annotation { "Feature Type Name" : "Feature", "Feature Type Description" : "" }
export const myFeature = defineFeature(function(context is Context, id is Id, definition is map)
    precondition{}
    {
        {
            var Q0;
            Q0=qCreatedBy(makeId("Front.planeOp"),FACE);
            var sketch = newSketch(context, id + "F0", { "sketchPlane" : qUnion([Q0])});
            skLineSegment(sketch, "E0", {"start": v(-61.48, 18.28) * mm, "end": v(-20.16, 18.28) * mm});
            skArc(sketch, "E1", {"start": v(-17.8, 28.55) * mm, "mid": v(-19.73, 23.59) * mm, "end": v(-20.16, 18.28) * mm});
            skArc(sketch, "E2", {"start": v(11.9, 28.55) * mm, "mid": v(-2.95, 29.61) * mm, "end": v(-17.8, 28.55) * mm});
            skArc(sketch, "E3", {"start": v(29.68, 17.53) * mm, "mid": v(21.17, 23.67) * mm, "end": v(11.9, 28.55) * mm});
            skArc(sketch, "E4", {"start": v(56.72, 13.52) * mm, "mid": v(43.38, 16.77) * mm, "end": v(29.68, 17.53) * mm});
            skArc(sketch, "E5", {"start": v(56.72, 13.52) * mm, "mid": v(57.23, 9.12) * mm, "end": v(58.87, 5) * mm});
            skArc(sketch, "E6", {"start": v(58.87, -5) * mm, "mid": v(60.21, 0) * mm, "end": v(58.87, 5) * mm});
            skArc(sketch, "E7", {"start": v(52.46, -2) * mm, "mid": v(55.3, -4.3) * mm, "end": v(58.87, -5) * mm});
            skArc(sketch, "E8", {"start": v(48.2, -13.52) * mm, "mid": v(51.2, -8.08) * mm, "end": v(52.46, -2) * mm});
            skArc(sketch, "E9", {"start": v(31.18, -5) * mm, "mid": v(37.02, -14.6) * mm, "end": v(48.2, -13.52) * mm});
            skLineSegment(sketch, "E10", {"start": v(31.18, -5) * mm, "end": v(-25.42, -5) * mm});
            skArc(sketch, "E11", {"start": v(-47.96, -5) * mm, "mid": v(-36.69, -14.8) * mm, "end": v(-25.42, -5) * mm});
            skArc(sketch, "E12", {"start": v(-55.47, -2.5) * mm, "mid": v(-52, -4.6) * mm, "end": v(-47.96, -5) * mm});
            skLineSegment(sketch, "E13", {"start": v(-55.47, -2.5) * mm, "end": v(-64.48, -2.5) * mm});
            skLineSegment(sketch, "E14", {"start": v(-64.48, -2.5) * mm, "end": v(-64.48, 3) * mm});
            skLineSegment(sketch, "E15", {"start": v(-64.48, 3) * mm, "end": v(-61.98, 3) * mm});
            skLineSegment(sketch, "E16", {"start": v(-61.98, 3) * mm, "end": v(-61.48, 18.28) * mm});
            skSolve(sketch);
        }
        {
            var Q0;
            Q0=makeQuery(id+"F0.imprint","IMPRINT",FACE,{"disambiguationData":[TD([[makeQuery(id+"F0.imprint","IMPRINT",EDGE,{"derivedFrom":sQuery(id+"F0.wireOp",EDGE,"E0")}),-1.0]])]});
            extrude(context, id + "F1", {"entities" : qUnion([Q0]), "depth" : 50.8 * mm, "offsetDistance" : 25.4 * mm});
        }
        {
            var Q0;
            Q0=makeQuery(id+"F1.opExtrude","SWEPT_FACE",FACE,{"disambiguationData":[OSD([sQuery(id+"F0.wireOp",EDGE,"E10")])]});
            var sketch = newSketch(context, id + "F2", { "sketchPlane" : qUnion([Q0])});
            skLineSegment(sketch, "E17.bottom", {"start": v(-47.4, 45.72) * mm, "end": v(52.99, 45.72) * mm});
            skLineSegment(sketch, "E17.top", {"start": v(-47.4, 5.08) * mm, "end": v(52.99, 5.08) * mm});
            skLineSegment(sketch, "E17.left", {"start": v(-47.4, 45.72) * mm, "end": v(-47.4, 5.08) * mm});
            skLineSegment(sketch, "E17.right", {"start": v(52.99, 45.72) * mm, "end": v(52.99, 5.08) * mm});
            skSolve(sketch);
        }
        {
            var Q0;
            Q0 = qSketchRegion(id + "F2", true);
            extrude(context, id + "F3", {"entities" : qUnion([Q0]), "operationType" : NewBodyOperationType.REMOVE, "depth" : 25.4 * mm, "offsetDistance" : 25.4 * mm});
        }
        {
            var Q0;
            Q0=makeQuery(id+"F1.opExtrude","SWEPT_FACE",FACE,{"disambiguationData":[OSD([sQuery(id+"F0.wireOp",EDGE,"E16")])]});
            var sketch = newSketch(context, id + "F4", { "sketchPlane" : qUnion([Q0])});
            skText(sketch, "E18", { "text": "Mason Hrdlicka", "fontName": "OpenSans-Regular.ttf"});
            const initialGuessF4  = {"E18": [0.00381, 0.00216, 1, 0, 0.0043]};
            skSetInitialGuess(sketch, initialGuessF4);
            skSolve(sketch);
        }
        {
            var Q0;
            Q0=makeQuery(id+"F1.opExtrude","CAP_EDGE",EDGE,{"disambiguationData":[OSD([sQuery(id+"F0.wireOp",EDGE,"E0")])],"isStart":false});
            var Q1;
            Q1=makeQuery(id+"F1.opExtrude","CAP_EDGE",EDGE,{"disambiguationData":[OSD([sQuery(id+"F0.wireOp",EDGE,"E16")])],"isStart":false});
            var Q2;
            Q2=makeQuery(id+"F1.opExtrude","SWEPT_EDGE",EDGE,{"disambiguationData":[OSD([sQuery(id+"F0.wireOp",EDGE,"E0"),sQuery(id+"F0.wireOp",EDGE,"E16")])]});
            var Q3;
            Q3=makeQuery(id+"F1.opExtrude","CAP_EDGE",EDGE,{"disambiguationData":[OSD([sQuery(id+"F0.wireOp",EDGE,"E16")])],"isStart":true});
            var Q4;
            Q4=makeQuery(id+"F1.opExtrude","CAP_EDGE",EDGE,{"disambiguationData":[OSD([sQuery(id+"F0.wireOp",EDGE,"E0")])],"isStart":true});
            fillet(context, id + "F5", {"entities" : qUnion([Q0, Q1, Q2, Q3, Q4]), "tangentPropagation" : true, "radius" : 5.08 * mm, "defaultsChanged" : false, "vertexSettings" : [], "allowEdgeOverflow" : false});
        }
        {
            var Q0;
            Q0 = qSketchRegion(id + "F4", true);
            extrude(context, id + "F6", {"entities" : qUnion([Q0]), "operationType" : NewBodyOperationType.REMOVE, "oppositeDirection" : true, "depth" : 0.25 * mm, "offsetDistance" : 25.4 * mm});
        }
    });